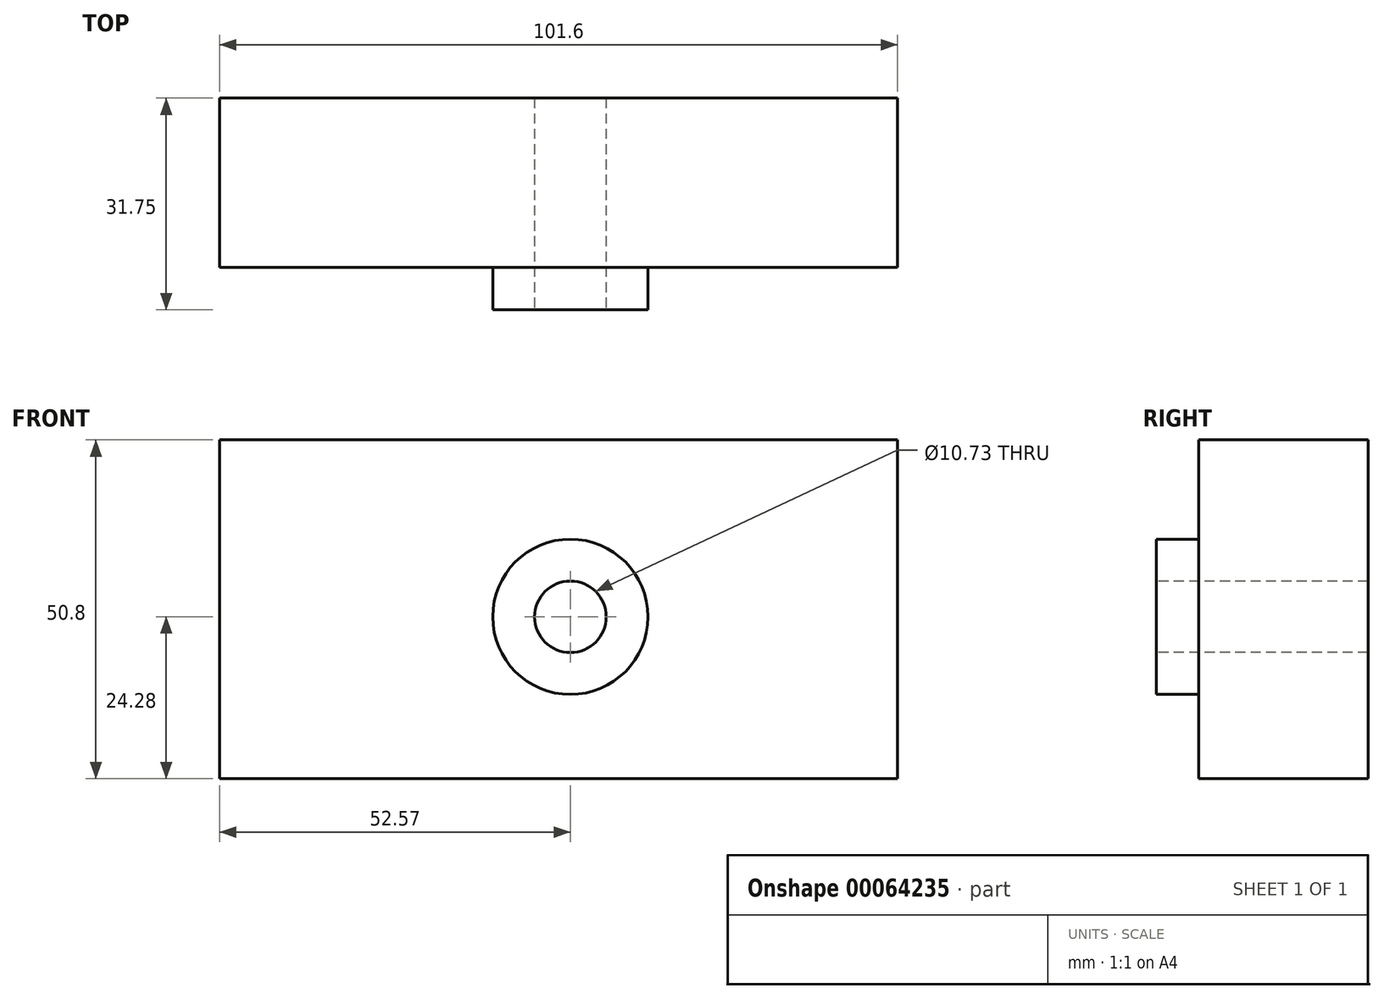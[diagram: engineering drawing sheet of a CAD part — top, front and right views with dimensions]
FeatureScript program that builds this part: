
annotation { "Feature Type Name" : "Feature", "Feature Type Description" : "" }
export const myFeature = defineFeature(function(context is Context, id is Id, definition is map)
    precondition{}
    {
        {
            var Q0;
            Q0=qCreatedBy(makeId("Front.planeOp"),FACE);
            var sketch = newSketch(context, id + "F0", { "sketchPlane" : qUnion([Q0])});
            skLineSegment(sketch, "E0.bottom", {"start": v(49.03, -24.28) * mm, "end": v(-52.57, -24.28) * mm});
            skLineSegment(sketch, "E0.top", {"start": v(49.03, 26.52) * mm, "end": v(-52.57, 26.52) * mm});
            skLineSegment(sketch, "E0.left", {"start": v(49.03, -24.28) * mm, "end": v(49.03, 26.52) * mm});
            skLineSegment(sketch, "E0.right", {"start": v(-52.57, -24.28) * mm, "end": v(-52.57, 26.52) * mm});
            skSolve(sketch);
        }
        {
            var Q0;
            Q0=makeQuery(id+"F0.imprint","IMPRINT",FACE,{"disambiguationData":[TD([[makeQuery(id+"F0.imprint","IMPRINT",EDGE,{"derivedFrom":sQuery(id+"F0.wireOp",EDGE,"E0.bottom")}),-1.0]])]});
            extrude(context, id + "F1", {"entities" : qUnion([Q0]), "depth" : 25.4 * mm});
        }
        {
            var Q0;
            Q0=makeQuery(id+"F1.opExtrude","CAP_FACE",FACE,{"disambiguationData":[OSD([sQuery(id+"F0.wireOp",EDGE,"E0.bottom"),sQuery(id+"F0.wireOp",EDGE,"E0.top"),sQuery(id+"F0.wireOp",EDGE,"E0.left"),sQuery(id+"F0.wireOp",EDGE,"E0.right")])],"isStart":false});
            var sketch = newSketch(context, id + "F2", { "sketchPlane" : qUnion([Q0])});
            skCircle(sketch, "E1", {"center": v(0, 0) * mm, "radius": 11.64 * mm});
            skSolve(sketch);
        }
        {
            var Q0;
            Q0=makeQuery(id+"F2.imprint","IMPRINT",FACE,{"disambiguationData":[TD([[makeQuery(id+"F2.imprint","IMPRINT",EDGE,{"derivedFrom":sQuery(id+"F2.wireOp",EDGE,"E1")}),1.0]])]});
            extrude(context, id + "F3", {"entities" : qUnion([Q0]), "operationType" : NewBodyOperationType.ADD, "depth" : 6.35 * mm});
        }
        {
            var Q0;
            Q0=makeQuery(id+"F3.opExtrude","CAP_FACE",FACE,{"disambiguationData":[OSD([sQuery(id+"F2.wireOp",EDGE,"E1")])],"isStart":false});
            var sketch = newSketch(context, id + "F4", { "sketchPlane" : qUnion([Q0])});
            skCircle(sketch, "E2", {"center": v(0, 0) * mm, "radius": 5.36 * mm});
            skSolve(sketch);
        }
        {
            var Q0;
            Q0=makeQuery(id+"F4.imprint","IMPRINT",FACE,{"disambiguationData":[TD([[makeQuery(id+"F4.imprint","IMPRINT",EDGE,{"derivedFrom":sQuery(id+"F4.wireOp",EDGE,"E2")}),1.0]])]});
            var Q1;
            Q1=makeQuery(id+"F1.opExtrude","SWEPT_FACE",FACE,{"disambiguationData":[OSD([sQuery(id+"F0.wireOp",EDGE,"E0.top")])]});
            extrude(context, id + "F5", {"entities" : qUnion([Q0]), "operationType" : NewBodyOperationType.REMOVE, "endBound" : BoundingType.THROUGH_ALL, "oppositeDirection" : true, "endBoundEntityFace" : qUnion([Q1]), "depth" : 47.75 * mm});
        }
    });
